# Revit family: Cabinet-Medicine-Kohler-99895_and_3073
name_source: partatom
category: Furniture
revit_build: Autodesk Revit MEP 2012 (Build: 20110916_2132(x64)
units: mm (PartAtom-declared; Revit-internal decimal feet)

## types (2) — shared parameters
Date Modified = January 26, 2015
Default Elevation = 48 "
Depth = 4.813 "
Equipment Abbreviation = MC
Family Version = 1.0
Height = 31 "
Manufacturer = Kohler Company
Model Disclaimer = Contact Kohler Company For More Information
Product Material = Aluminum - Kohler - Anodized
Product Page URL = http://www.us.kohler.com
URL = http://www.us.kohler.com
Width = 20 "
zz Length 2 = 4.813 "
zz Length 4 = 31 "
zz Length 7 = 20 "

## per-type parameters (varying)
| type | Description | Model | zz Integer 1 | zz YesNo 2 |
| Standard | Archer Aluminum Single-Door Medicine Cabinet | K-99895-NA | 1 | No |
| Beveled | Archer Aluminum Single-Door Medicine Cabinet, Beveled Edge | K-3073-NA | 2 | Yes |

## geometry (parser evidence)
native form markers: Blend x2, Sweep x4
no freeform markers — native parametric forms only
